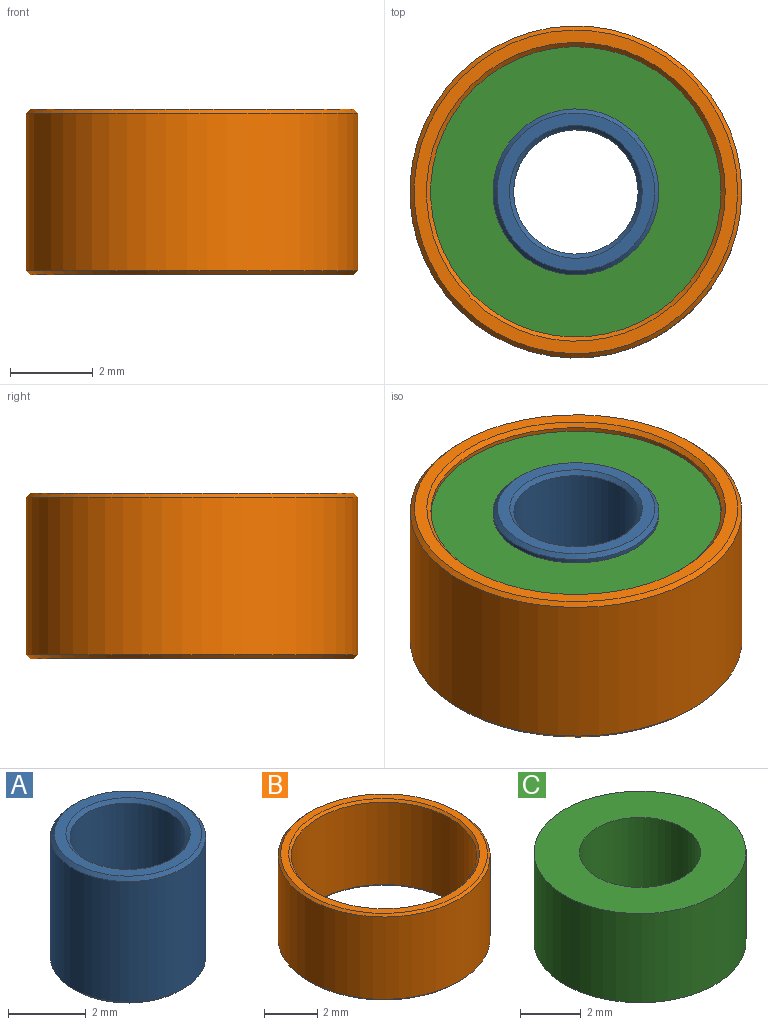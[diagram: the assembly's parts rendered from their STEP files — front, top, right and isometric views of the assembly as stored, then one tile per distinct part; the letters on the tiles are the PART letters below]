
ASSEMBLY  parts=3 mates=2
PART A: 8 faces, bbox 4x4x4 mm
  f0: cylinder r=1.5mm len=3.8mm, axis (0,0,-1), area 35.8mm2, adj f5,f7
  f1: cylinder r=2mm len=4mm, axis (0,0,-1), area 47.8mm2, adj f4,f6
  f2: plane 3.8x3.8mm, normal (0,0,1), area 3.3mm2, adj f4,f5
  f3: plane 3.8x3.8mm, normal (0,0,-1), area 3.3mm2, adj f6,f7
  f4: cone r=1.9mm half-angle=45deg, axis (0,0,-1), area 1.7mm2, adj f1,f2
  f5: cone r=1.5mm half-angle=45deg, axis (0,0,1), area 1.4mm2, adj f0,f2
  f6: cone r=2mm half-angle=45deg, axis (0,0,1), area 1.7mm2, adj f1,f3
  f7: cone r=1.6mm half-angle=45deg, axis (0,0,-1), area 1.4mm2, adj f0,f3
PART B: 8 faces, bbox 8x8x4 mm
  f0: cylinder r=3.5mm len=7mm, axis (0,0,-1), area 83.6mm2, adj f4,f6
  f1: cylinder r=4mm len=8mm, axis (0,0,-1), area 95.5mm2, adj f5,f7
  f2: plane 7.8x7.8mm, normal (0,0,1), area 7.1mm2, adj f4,f5
  f3: plane 7.8x7.8mm, normal (0,0,-1), area 7.1mm2, adj f6,f7
  f4: cone r=3.5mm half-angle=45deg, axis (0,0,1), area 3.2mm2, adj f0,f2
  f5: cone r=3.9mm half-angle=45deg, axis (0,0,-1), area 3.5mm2, adj f1,f2
  f6: cone r=3.6mm half-angle=45deg, axis (0,0,-1), area 3.2mm2, adj f0,f3
  f7: cone r=4mm half-angle=45deg, axis (0,0,1), area 3.5mm2, adj f1,f3
PART C: 4 faces, bbox 7x7x3.6 mm
  f0: cylinder r=2mm len=4mm, axis (0,0,-1), area 45.2mm2, adj f2,f3
  f1: cylinder r=3.5mm len=7mm, axis (0,0,-1), area 79.2mm2, adj f2,f3
  f2: plane 7x7mm, normal (0,0,1), area 25.9mm2, adj f0,f1
  f3: plane 7x7mm, normal (0,0,-1), area 25.9mm2, adj f0,f1
PLACE A at identity
PLACE B at identity
PLACE C at identity
MATE fastened A.f0 <-> B.f0  axis (0,0,-1) through (0,0,0)mm
MATE fastened A.f0 <-> C.f0  axis (0,0,-1) through (0,0,0)mm
